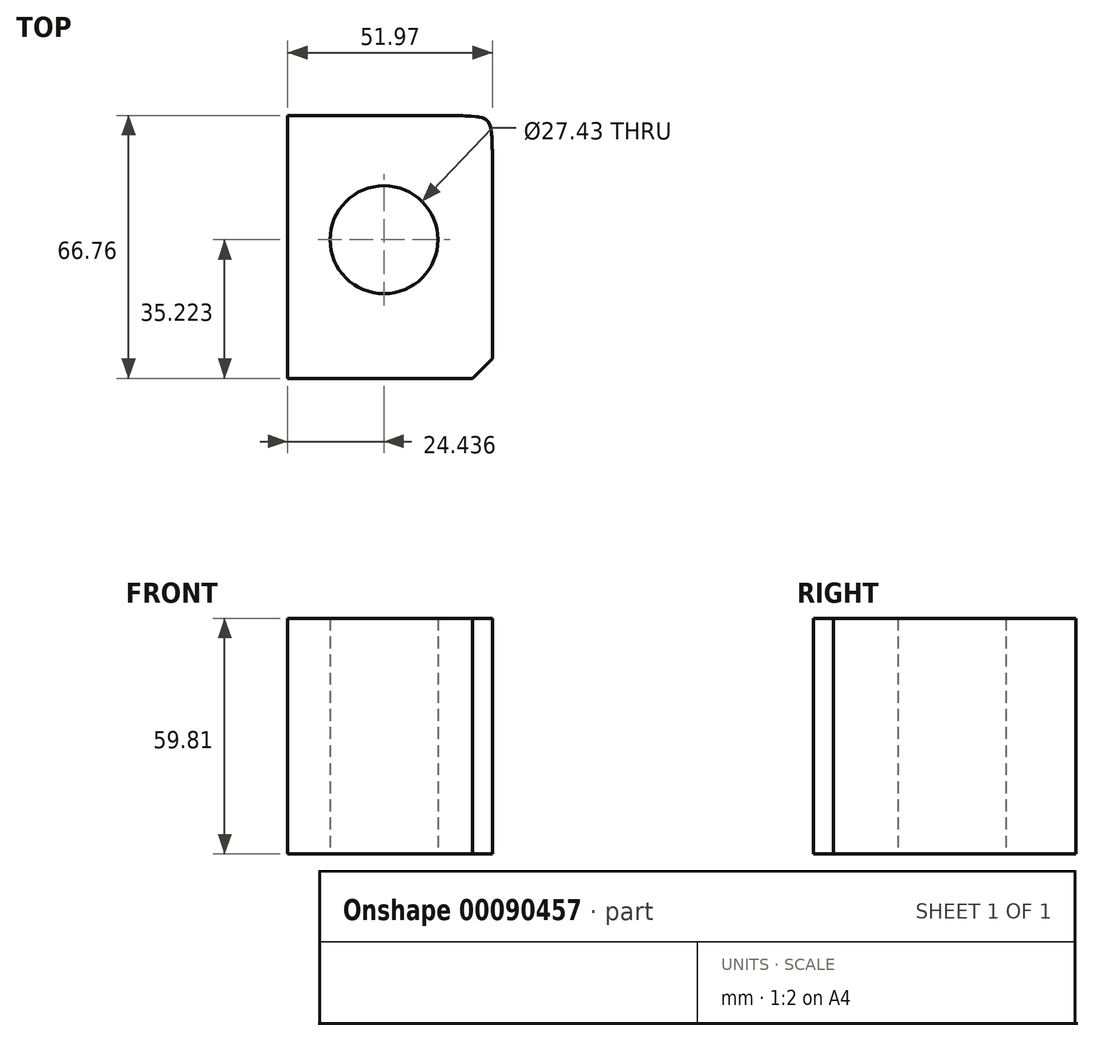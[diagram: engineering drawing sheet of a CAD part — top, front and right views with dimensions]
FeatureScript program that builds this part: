
annotation { "Feature Type Name" : "Feature", "Feature Type Description" : "" }
export const myFeature = defineFeature(function(context is Context, id is Id, definition is map)
    precondition{}
    {
        {
            var Q0;
            Q0=qCreatedBy(makeId("Top.planeOp"),FACE);
            var sketch = newSketch(context, id + "F0", { "sketchPlane" : qUnion([Q0])});
            skLineSegment(sketch, "E0.bottom", {"start": v(0, 0) * mm, "end": v(51.97, 0) * mm});
            skLineSegment(sketch, "E0.top", {"start": v(0, 66.76) * mm, "end": v(51.97, 66.76) * mm});
            skLineSegment(sketch, "E0.left", {"start": v(0, 0) * mm, "end": v(0, 66.76) * mm});
            skLineSegment(sketch, "E0.right", {"start": v(51.97, 0) * mm, "end": v(51.97, 66.76) * mm});
            skCircle(sketch, "E1", {"center": v(24.44, 35.22) * mm, "radius": 13.71 * mm});
            skSolve(sketch);
        }
        {
            var Q0;
            Q0 = qSketchRegion(id + "F0", true);
            extrude(context, id + "F1", {"entities" : qUnion([Q0]), "depth" : 59.8 * mm});
        }
        {
            var Q0;
            Q0=makeQuery(id+"F1.opExtrude","SWEPT_EDGE",EDGE,{"disambiguationData":[OSD([sQuery(id+"F0.wireOp",EDGE,"E0.bottom"),sQuery(id+"F0.wireOp",EDGE,"E0.right")])]});
            chamfer(context, id + "F2", {"entities" : qUnion([Q0]), "width" : 5.08 * mm, "tangentPropagation" : true});
        }
        {
            var Q0;
            Q0=makeQuery(id+"F1.opExtrude","SWEPT_EDGE",EDGE,{"disambiguationData":[OSD([sQuery(id+"F0.wireOp",EDGE,"E0.top"),sQuery(id+"F0.wireOp",EDGE,"E0.right")])]});
            fillet(context, id + "F3", {"entities" : qUnion([Q0]), "radius" : 12.7 * mm, "tangentPropagation" : true, "rho" : .8, "crossSection" : FilletCrossSection.CONIC, "allowEdgeOverflow" : false});
        }
    });
